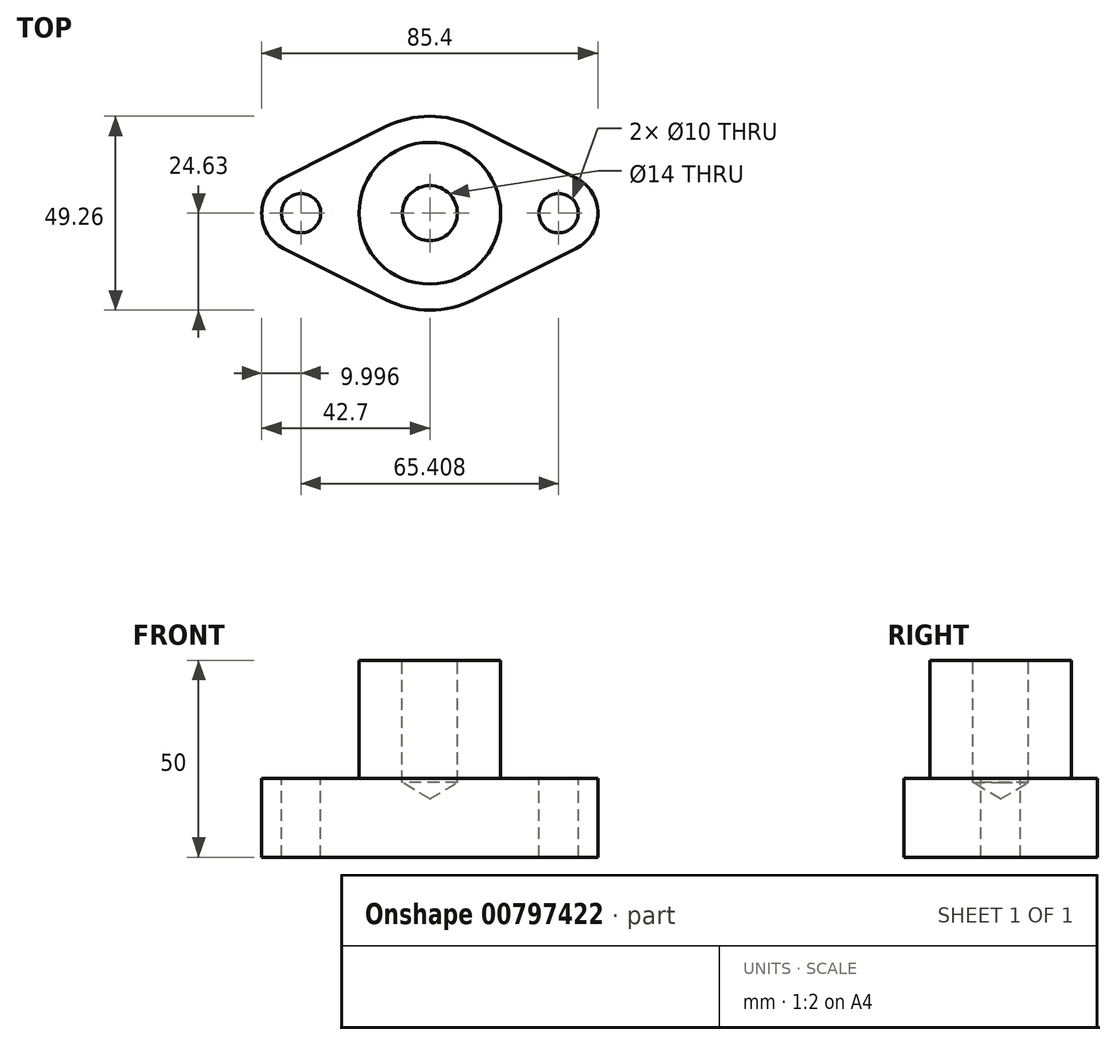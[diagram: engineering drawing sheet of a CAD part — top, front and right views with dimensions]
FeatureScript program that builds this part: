
annotation { "Feature Type Name" : "Feature", "Feature Type Description" : "" }
export const myFeature = defineFeature(function(context is Context, id is Id, definition is map)
    precondition{}
    {
        {
            var Q0;
            Q0=qCreatedBy(makeId("Top.planeOp"),FACE);
            var sketch = newSketch(context, id + "F0", { "sketchPlane" : qUnion([Q0])});
            skLineSegment(sketch, "E0", {"start": v(-55, 0) * mm, "end": v(0, 27.6) * mm});
            skLineSegment(sketch, "E1", {"start": v(0, 27.6) * mm, "end": v(55, 0) * mm});
            skLineSegment(sketch, "E2", {"start": v(55, 0) * mm, "end": v(0, -27.6) * mm});
            skLineSegment(sketch, "E3", {"start": v(0, -27.6) * mm, "end": v(-55, 0) * mm});
            skSolve(sketch);
        }
        {
            var Q0;
            Q0=makeQuery(id+"F0.imprint","IMPRINT",FACE,{"disambiguationData":[TD([[makeQuery(id+"F0.imprint","IMPRINT",EDGE,{"derivedFrom":sQuery(id+"F0.wireOp",EDGE,"E0")}),-1.0]])]});
            extrude(context, id + "F1", {"entities" : qUnion([Q0]), "depth" : 20 * mm, "offsetDistance" : 25 * mm});
        }
        {
            var Q0;
            Q0=makeQuery(id+"F1.opExtrude","SWEPT_EDGE",EDGE,{"disambiguationData":[OSD([sQuery(id+"F0.wireOp",EDGE,"E1"),sQuery(id+"F0.wireOp",EDGE,"E2")])]});
            var Q1;
            Q1=makeQuery(id+"F1.opExtrude","SWEPT_EDGE",EDGE,{"disambiguationData":[OSD([sQuery(id+"F0.wireOp",EDGE,"E0"),sQuery(id+"F0.wireOp",EDGE,"E3")])]});
            fillet(context, id + "F2", {"entities" : qUnion([Q0, Q1]), "radius" : 10 * mm, "tangentPropagation" : true, "allowEdgeOverflow" : false});
        }
        {
            var Q0;
            Q0=makeQuery(id+"F1.opExtrude","SWEPT_EDGE",EDGE,{"disambiguationData":[OSD([sQuery(id+"F0.wireOp",EDGE,"E2"),sQuery(id+"F0.wireOp",EDGE,"E3")])]});
            var Q1;
            Q1=makeQuery(id+"F1.opExtrude","SWEPT_EDGE",EDGE,{"disambiguationData":[OSD([sQuery(id+"F0.wireOp",EDGE,"E0"),sQuery(id+"F0.wireOp",EDGE,"E1")])]});
            fillet(context, id + "F3", {"entities" : qUnion([Q0, Q1]), "radius" : 25 * mm, "tangentPropagation" : true, "allowEdgeOverflow" : false});
        }
        {
            var Q0;
            Q0=makeQuery(id+"F1.opExtrude","CAP_FACE",FACE,{"disambiguationData":[OSD([sQuery(id+"F0.wireOp",EDGE,"E0"),sQuery(id+"F0.wireOp",EDGE,"E1"),sQuery(id+"F0.wireOp",EDGE,"E2"),sQuery(id+"F0.wireOp",EDGE,"E3")])],"isStart":false});
            var sketch = newSketch(context, id + "F4", { "sketchPlane" : qUnion([Q0])});
            skPoint(sketch, "E4", {"position": v(-32.7, 0) * mm});
            skPoint(sketch, "E5", {"position": v(32.7, 0) * mm});
            skPoint(sketch, "E6", {"position": v(0, 0) * mm});
            skCircle(sketch, "E7", {"center": v(0, 0) * mm, "radius": 18 * mm});
            skSolve(sketch);
        }
        {
            var Q0;
            Q0=makeQuery(id+"F4.imprint","IMPRINT",FACE,{"disambiguationData":[TD([[makeQuery(id+"F4.imprint","IMPRINT",EDGE,{"derivedFrom":sQuery(id+"F4.wireOp",EDGE,"E7")}),1.0]])]});
            extrude(context, id + "F5", {"entities" : qUnion([Q0]), "operationType" : NewBodyOperationType.ADD, "depth" : 30 * mm, "offsetDistance" : 25 * mm});
        }
        {
            var Q0;
            Q0=makeQuery(id+"F1.opExtrude","CAP_FACE",FACE,{"disambiguationData":[OSD([sQuery(id+"F0.wireOp",EDGE,"E0"),sQuery(id+"F0.wireOp",EDGE,"E1"),sQuery(id+"F0.wireOp",EDGE,"E2"),sQuery(id+"F0.wireOp",EDGE,"E3")])],"isStart":false});
            var sketch = newSketch(context, id + "F6", { "sketchPlane" : qUnion([Q0])});
            skPoint(sketch, "E8", {"position": v(-32.7, 0) * mm});
            skPoint(sketch, "E9", {"position": v(32.7, 0) * mm});
            skPoint(sketch, "E10", {"position": v(0, 0) * mm});
            skSolve(sketch);
        }
        {
            var Q0;
            Q0=sQuery(id+"F6.wireOp",VERTEX,"E8");
            var Q1;
            Q1=sQuery(id+"F6.wireOp",VERTEX,"E9");
            var Q2;
            Q2=makeQuery(id+"F1.opExtrude","SWEPT_BODY",BODY,{"disambiguationData":[OSD([sQuery(id+"F0.wireOp",EDGE,"E0"),sQuery(id+"F0.wireOp",EDGE,"E1"),sQuery(id+"F0.wireOp",EDGE,"E2"),sQuery(id+"F0.wireOp",EDGE,"E3")])]});
            hole(context, id + "F7", {"style" : HoleStyle.SIMPLE, "endStyle" : HoleEndStyle.THROUGH, "holeDiameter" : 10 * mm, "majorDiameter" : 5 * mm, "isTappedThrough" : true, "tappedDepth" : 12 * mm, "tapClearance" : 3, "locations" : qUnion([Q0, Q1]), "scope" : qUnion([Q2])});
        }
        {
            var Q0;
            Q0=makeQuery(id+"F5.opExtrude","CAP_FACE",FACE,{"disambiguationData":[OSD([sQuery(id+"F4.wireOp",EDGE,"E7")])],"isStart":false});
            var sketch = newSketch(context, id + "F8", { "sketchPlane" : qUnion([Q0])});
            skPoint(sketch, "E11", {"position": v(0, 0) * mm});
            skSolve(sketch);
        }
        {
            var Q0;
            Q0=sQuery(id+"F8.wireOp",VERTEX,"E11");
            var Q1;
            Q1=makeQuery(id+"F1.opExtrude","SWEPT_BODY",BODY,{"disambiguationData":[OSD([sQuery(id+"F0.wireOp",EDGE,"E0"),sQuery(id+"F0.wireOp",EDGE,"E1"),sQuery(id+"F0.wireOp",EDGE,"E2"),sQuery(id+"F0.wireOp",EDGE,"E3")])]});
            hole(context, id + "F9", {"style" : HoleStyle.SIMPLE, "endStyle" : HoleEndStyle.BLIND, "standardTappedOrClearance" : lookupTablePath({ "standard" : "ISO", "engagement" : "75%", "pitch" : "2 mm", "size" : "M16", "type" : "Tapped" }), "standardBlindInLast" : lookupTablePath({ "standard" : "ISO", "engagement" : "75%", "pitch" : "2 mm", "size" : "M16", "type" : "Tapped" }), "holeDiameter" : 14 * mm, "majorDiameter" : 16 * mm, "showTappedDepth" : true, "holeDepth" : 31 * mm, "isTappedThrough" : true, "tappedDepth" : 25 * mm, "tapClearance" : 3, "locations" : qUnion([Q0]), "scope" : qUnion([Q1])});
        }
    });
